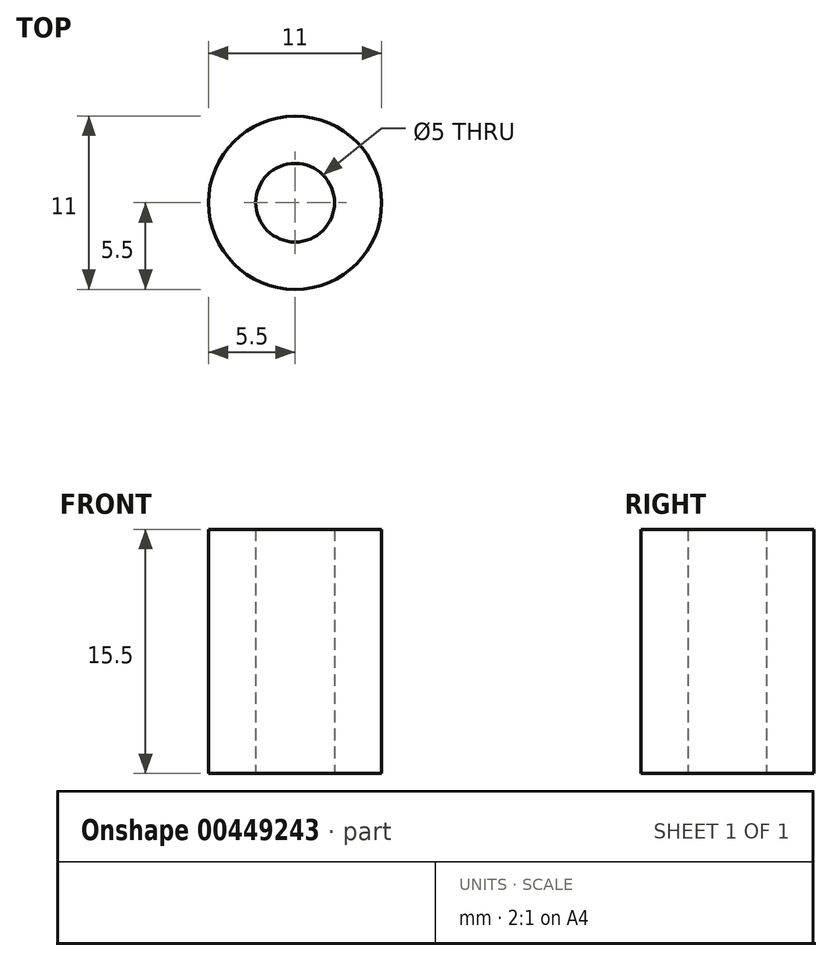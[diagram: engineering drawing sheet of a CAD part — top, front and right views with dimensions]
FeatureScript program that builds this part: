
annotation { "Feature Type Name" : "Feature", "Feature Type Description" : "" }
export const myFeature = defineFeature(function(context is Context, id is Id, definition is map)
    precondition{}
    {
        {
            var Q0;
            Q0=qCreatedBy(makeId("Top.planeOp"),FACE);
            var sketch = newSketch(context, id + "F0", { "sketchPlane" : qUnion([Q0])});
            skCircle(sketch, "E0", {"center": v(0, 0) * mm, "radius": 5.5 * mm});
            skCircle(sketch, "E1", {"center": v(0, 0) * mm, "radius": 2.5 * mm});
            skSolve(sketch);
        }
        {
            var Q0;
            Q0 = qSketchRegion(id + "F0", true);
            extrude(context, id + "F1", {"entities" : qUnion([Q0]), "depth" : 15.5 * mm});
        }
    });
